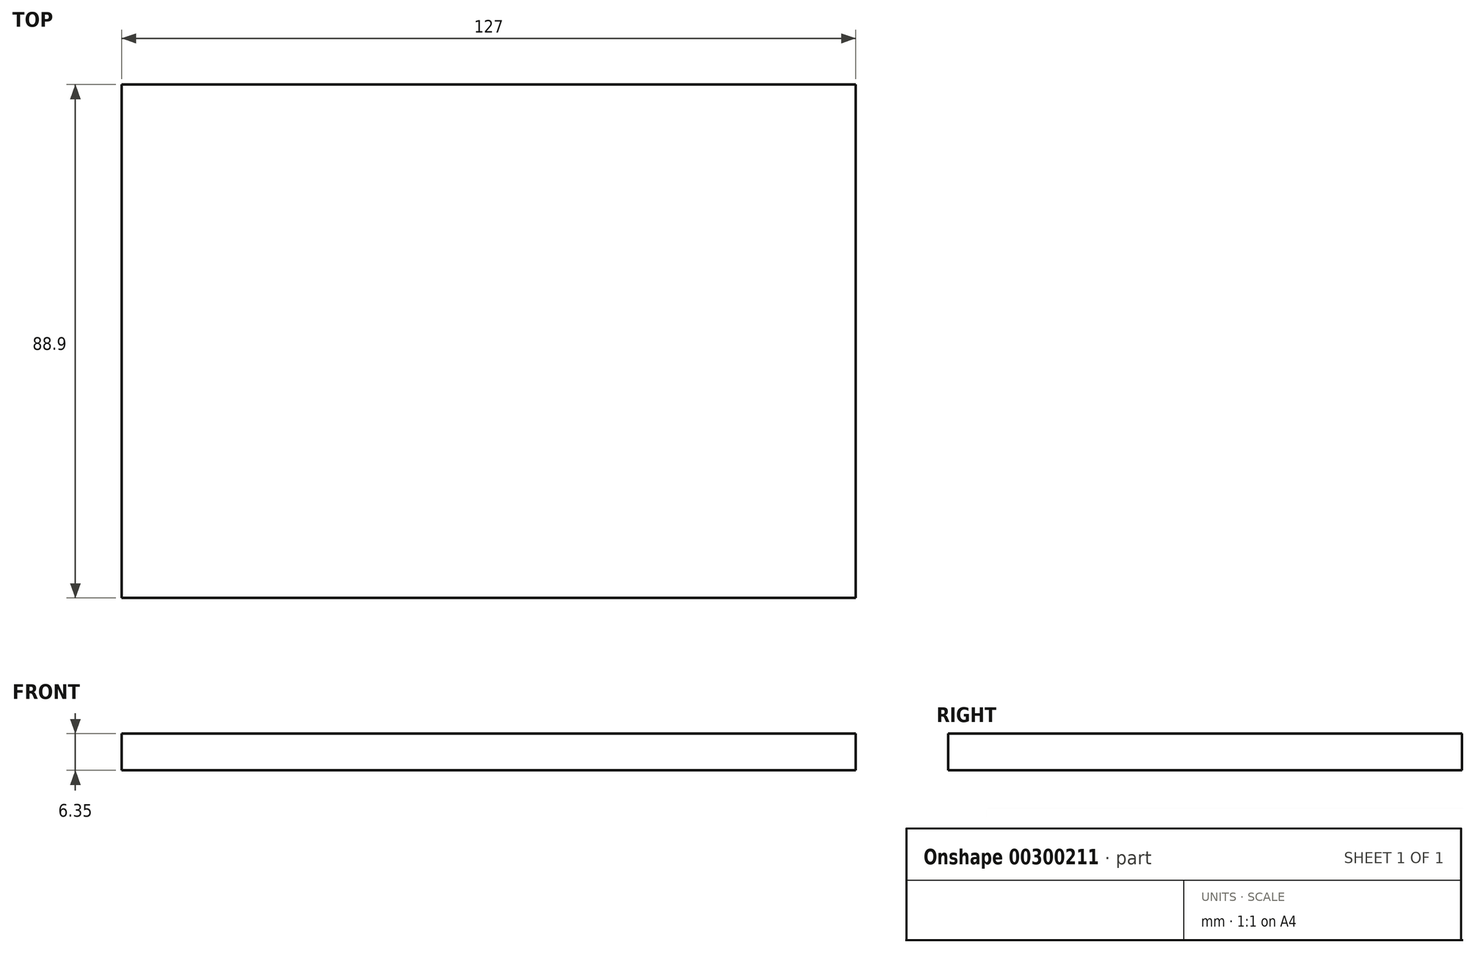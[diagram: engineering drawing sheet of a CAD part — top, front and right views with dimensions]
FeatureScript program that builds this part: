
annotation { "Feature Type Name" : "Feature", "Feature Type Description" : "" }
export const myFeature = defineFeature(function(context is Context, id is Id, definition is map)
    precondition{}
    {
        {
            var Q0;
            Q0=qCreatedBy(makeId("Top.planeOp"),FACE);
            var sketch = newSketch(context, id + "F0", { "sketchPlane" : qUnion([Q0])});
            skLineSegment(sketch, "E0.bottom", {"start": v(-89.61, 30.1) * mm, "end": v(37.39, 30.1) * mm});
            skLineSegment(sketch, "E0.top", {"start": v(-89.61, -58.8) * mm, "end": v(37.39, -58.8) * mm});
            skLineSegment(sketch, "E0.left", {"start": v(-89.61, 30.1) * mm, "end": v(-89.61, -58.8) * mm});
            skLineSegment(sketch, "E0.right", {"start": v(37.39, 30.1) * mm, "end": v(37.39, -58.8) * mm});
            skSolve(sketch);
        }
        {
            var Q0;
            Q0=makeQuery(id+"F0.imprint","IMPRINT",FACE,{"disambiguationData":[TD([[makeQuery(id+"F0.imprint","IMPRINT",EDGE,{"derivedFrom":sQuery(id+"F0.wireOp",EDGE,"E0.bottom")}),-1.0]])]});
            extrude(context, id + "F1", {"entities" : qUnion([Q0]), "depth" : 6.35 * mm});
        }
    });
